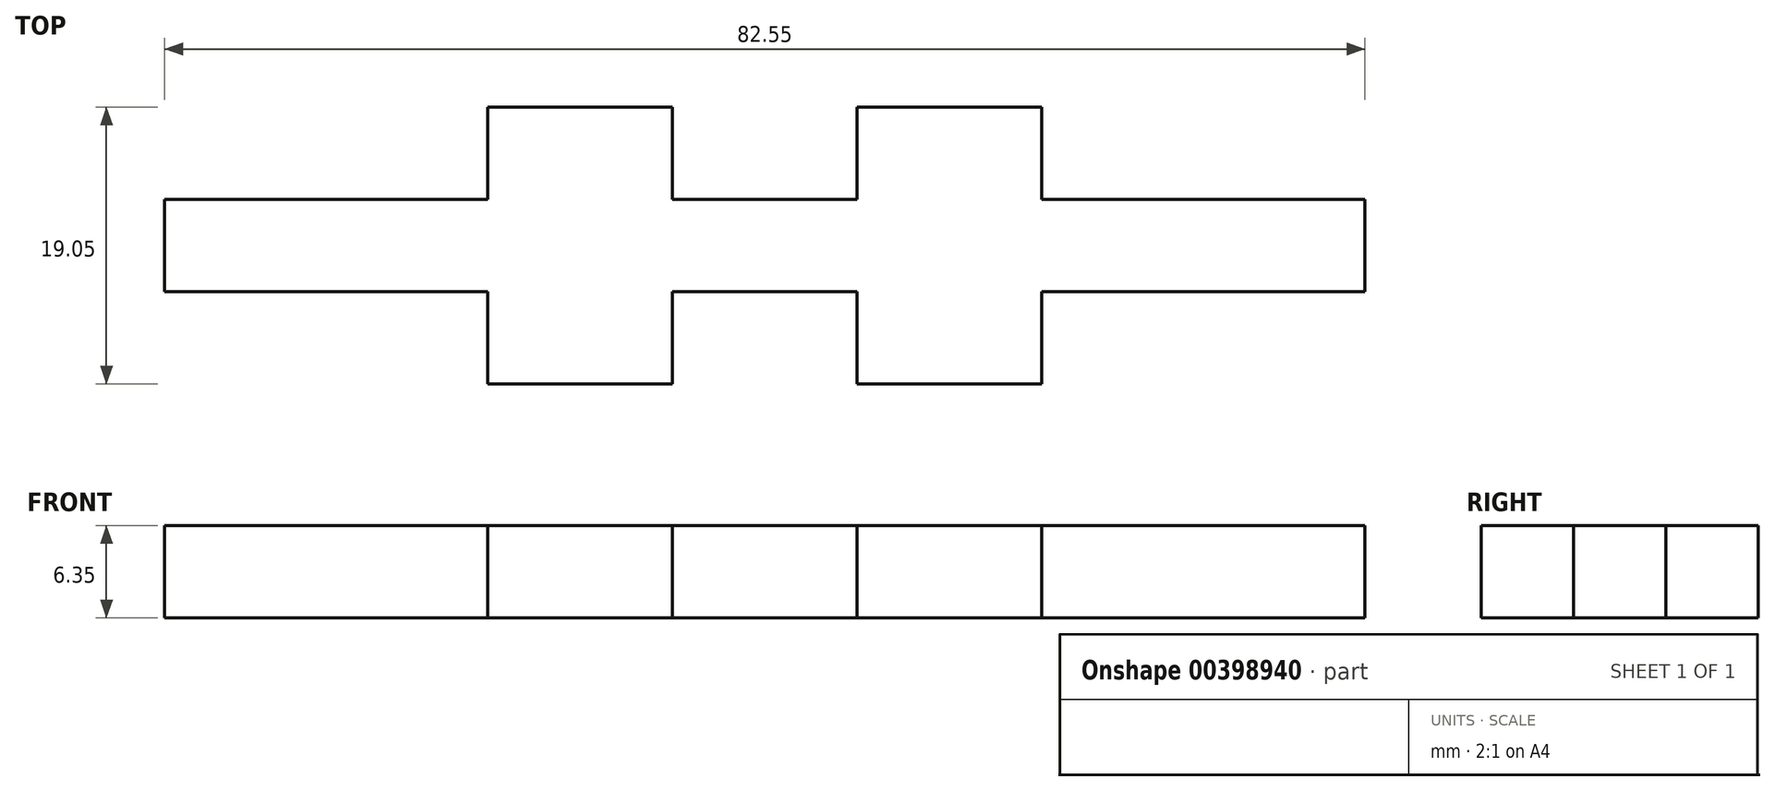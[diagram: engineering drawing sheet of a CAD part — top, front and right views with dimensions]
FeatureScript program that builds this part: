
annotation { "Feature Type Name" : "Feature", "Feature Type Description" : "" }
export const myFeature = defineFeature(function(context is Context, id is Id, definition is map)
    precondition{}
    {
        {
            var Q0;
            Q0=qCreatedBy(makeId("Top.planeOp"),FACE);
            var sketch = newSketch(context, id + "F0", { "sketchPlane" : qUnion([Q0])});
            skLineSegment(sketch, "E0.bottom", {"start": v(22.23, 0) * mm, "end": v(34.93, 0) * mm});
            skLineSegment(sketch, "E0.top", {"start": v(22.23, -19.05) * mm, "end": v(34.93, -19.05) * mm});
            skLineSegment(sketch, "E0.left", {"start": v(0, 0) * mm, "end": v(0, -12.7) * mm});
            skLineSegment(sketch, "E0.right", {"start": v(82.55, -6.35) * mm, "end": v(82.55, -12.7) * mm});
            skLineSegment(sketch, "E1", {"start": v(0, 0) * mm, "end": v(0, -6.35) * mm});
            skLineSegment(sketch, "E2", {"start": v(0, -6.35) * mm, "end": v(22.23, -6.35) * mm});
            skLineSegment(sketch, "E3", {"start": v(22.23, -6.35) * mm, "end": v(22.23, 0) * mm});
            skLineSegment(sketch, "E4", {"start": v(34.93, 0) * mm, "end": v(34.93, -6.35) * mm});
            skLineSegment(sketch, "E5", {"start": v(34.93, -6.35) * mm, "end": v(47.63, -6.35) * mm});
            skLineSegment(sketch, "E6", {"start": v(47.63, -6.35) * mm, "end": v(47.63, 0) * mm});
            skLineSegment(sketch, "E7", {"start": v(47.63, 0) * mm, "end": v(60.33, 0) * mm});
            skLineSegment(sketch, "E8", {"start": v(60.33, 0) * mm, "end": v(60.33, -6.35) * mm});
            skLineSegment(sketch, "E9", {"start": v(60.33, -6.35) * mm, "end": v(82.55, -6.35) * mm});
            skPoint(sketch, "E10.orphan", {"position": v(82.55, 0) * mm});
            skLineSegment(sketch, "E11", {"start": v(0, -6.35) * mm, "end": v(0, -12.7) * mm});
            skLineSegment(sketch, "E12", {"start": v(0, -12.7) * mm, "end": v(22.23, -12.7) * mm});
            skLineSegment(sketch, "E13", {"start": v(22.23, -12.7) * mm, "end": v(22.23, -19.05) * mm});
            skLineSegment(sketch, "E14", {"start": v(34.93, -19.05) * mm, "end": v(34.93, -12.7) * mm});
            skLineSegment(sketch, "E15", {"start": v(34.93, -12.7) * mm, "end": v(47.63, -12.7) * mm});
            skLineSegment(sketch, "E16", {"start": v(47.63, -12.7) * mm, "end": v(47.63, -19.05) * mm});
            skLineSegment(sketch, "E17", {"start": v(47.63, -19.05) * mm, "end": v(60.33, -19.05) * mm});
            skLineSegment(sketch, "E18", {"start": v(60.33, -19.05) * mm, "end": v(60.33, -12.7) * mm});
            skLineSegment(sketch, "E19", {"start": v(60.33, -12.7) * mm, "end": v(82.55, -12.7) * mm});
            skPoint(sketch, "E20.orphan", {"position": v(0, -19.05) * mm});
            skSolve(sketch);
        }
        {
            var Q0;
            Q0=makeQuery(id+"F0.imprint","IMPRINT",FACE,{"disambiguationData":[TD([[makeQuery(id+"F0.imprint","IMPRINT",EDGE,{"derivedFrom":sQuery(id+"F0.wireOp",EDGE,"E0.right")}),-1.0]])]});
            extrude(context, id + "F1", {"entities" : qUnion([Q0]), "depth" : 6.35 * mm, "offsetDistance" : 25.4 * mm});
        }
    });
